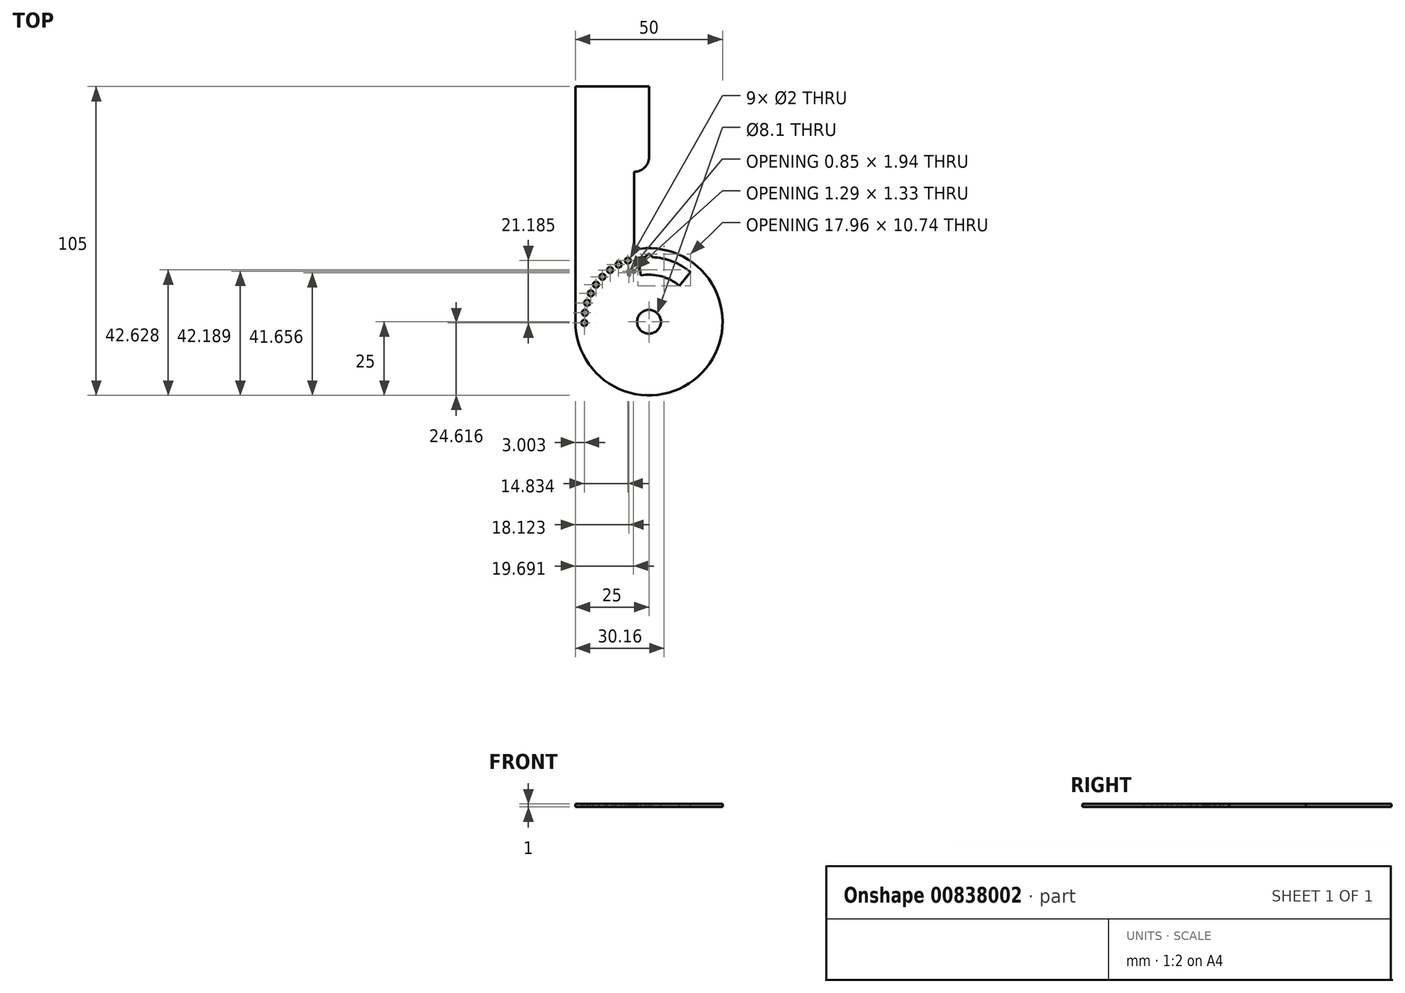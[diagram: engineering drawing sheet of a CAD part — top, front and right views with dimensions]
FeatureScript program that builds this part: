
annotation { "Feature Type Name" : "Feature", "Feature Type Description" : "" }
export const myFeature = defineFeature(function(context is Context, id is Id, definition is map)
    precondition{}
    {
        {
            var Q0;
            Q0=qCreatedBy(makeId("Top.planeOp"),FACE);
            var sketch = newSketch(context, id + "F0", { "sketchPlane" : qUnion([Q0])});
            skCircle(sketch, "E0", {"center": v(0, 0) * mm, "radius": 4.05 * mm});
            skCircle(sketch, "E1", {"center": v(0, 0) * mm, "radius": 25 * mm});
            skLineSegment(sketch, "E2.bottom", {"start": v(-25, 0) * mm, "end": v(25, 0) * mm});
            skLineSegment(sketch, "E2.top", {"start": v(-25, 80) * mm, "end": v(25, 80) * mm});
            skLineSegment(sketch, "E2.left", {"start": v(-25, 0) * mm, "end": v(-25, 80) * mm});
            skLineSegment(sketch, "E2.right", {"start": v(25, 0) * mm, "end": v(25, 80) * mm});
            skLineSegment(sketch, "E3.bottom", {"start": v(25, 65) * mm, "end": v(0, 65) * mm});
            skLineSegment(sketch, "E3.left", {"start": v(25, 65) * mm, "end": v(25, 35) * mm});
            skLineSegment(sketch, "E3.right", {"start": v(0, 65) * mm, "end": v(0, 60) * mm});
            skLineSegment(sketch, "E4", {"start": v(0, 60) * mm, "end": v(25, 35) * mm});
            skSolve(sketch);
        }
        {
            var Q0;
            {var subQ7=sQuery(id+"F0.wireOp",EDGE,"E2.top");Q0=makeQuery(id+"F0.imprint","IMPRINT",FACE,{"disambiguationData":[TD([[makeQuery(id+"F0.imprint","IMPRINT",EDGE,{"derivedFrom":subQ7}),-1.0]])]});}
            var Q1;
            {var subQ0=sQuery(id+"F0.wireOp",EDGE,"E2.bottom");var subQ1=sQuery(id+"F0.wireOp",EDGE,"E0");var subQ2=makeQuery(id+"F0.imprint","INTERSECT",VERTEX,{"disambiguationData":[OD(0.0)],"derivedFrom":[subQ1,subQ0]});Q1=makeQuery(id+"F0.imprint","IMPRINT",FACE,{"disambiguationData":[TD([[makeQuery(id+"F0.imprint","IMPRINT",EDGE,{"disambiguationData":[TD([[subQ2,1.0]])],"derivedFrom":subQ1}),-1.0]])]});}
            var Q2;
            {var subQ0=sQuery(id+"F0.wireOp",EDGE,"E2.bottom");var subQ1=sQuery(id+"F0.wireOp",EDGE,"E0");var subQ2=makeQuery(id+"F0.imprint","INTERSECT",VERTEX,{"disambiguationData":[OD(0.0)],"derivedFrom":[subQ1,subQ0]});Q2=makeQuery(id+"F0.imprint","IMPRINT",FACE,{"disambiguationData":[TD([[makeQuery(id+"F0.imprint","IMPRINT",EDGE,{"disambiguationData":[TD([[subQ2,-1.0]])],"derivedFrom":subQ1}),-1.0]])]});}
            var Q3;
            Q3=makeQuery(id+"F0.imprint","IMPRINT",FACE,{"disambiguationData":[TD([[makeQuery(id+"F0.imprint","IMPRINT",EDGE,{"derivedFrom":sQuery(id+"F0.wireOp",EDGE,"E3.bottom")}),1.0]])]});
            extrude(context, id + "F1", {"entities" : qUnion([Q0, Q1, Q2, Q3]), "oppositeDirection" : true, "depth" : 1 * mm, "offsetDistance" : 25 * mm});
        }
        {
            var Q0;
            Q0=makeQuery(id+"F1.opExtrude","CAP_FACE",FACE,{"disambiguationData":[OSD([sQuery(id+"F0.wireOp",EDGE,"E0"),sQuery(id+"F0.wireOp",EDGE,"E1"),sQuery(id+"F0.wireOp",EDGE,"E2.top"),sQuery(id+"F0.wireOp",EDGE,"E2.left"),sQuery(id+"F0.wireOp",EDGE,"E2.right"),sQuery(id+"F0.wireOp",EDGE,"E3.bottom"),sQuery(id+"F0.wireOp",EDGE,"E3.right"),sQuery(id+"F0.wireOp",EDGE,"E4")])],"isStart":true});
            var sketch = newSketch(context, id + "F2", { "sketchPlane" : qUnion([Q0])});
            skCircle(sketch, "E5", {"center": v(0, -22) * mm, "radius": 1 * mm});
            skPoint(sketch, "E5.centerSnap0", {"position": v(0, -25) * mm});
            skCircle(sketch, "E6.1.0", {"center": v(3.82, -21.67) * mm, "radius": 1 * mm});
            skCircle(sketch, "E6.2.0", {"center": v(7.52, -20.67) * mm, "radius": 1 * mm});
            skCircle(sketch, "E6.3.0", {"center": v(11, -19.05) * mm, "radius": 1 * mm});
            skCircle(sketch, "E6.4.0", {"center": v(14.14, -16.85) * mm, "radius": 1 * mm});
            skCircle(sketch, "E6.5.0", {"center": v(16.85, -14.14) * mm, "radius": 1 * mm});
            skCircle(sketch, "E6.6.0", {"center": v(19.05, -11) * mm, "radius": 1 * mm});
            skCircle(sketch, "E6.7.0", {"center": v(20.67, -7.52) * mm, "radius": 1 * mm});
            skCircle(sketch, "E6.8.0", {"center": v(21.67, -3.82) * mm, "radius": 1 * mm});
            skCircle(sketch, "E6.9.0", {"center": v(22, 0) * mm, "radius": 1 * mm});
            skCircle(sketch, "E6.10.0", {"center": v(21.67, 3.82) * mm, "radius": 1 * mm});
            skCircle(sketch, "E6.11.0", {"center": v(20.67, 7.52) * mm, "radius": 1 * mm});
            skCircle(sketch, "E6.12.0", {"center": v(19.05, 11) * mm, "radius": 1 * mm});
            skCircle(sketch, "E6.13.0", {"center": v(16.85, 14.14) * mm, "radius": 1 * mm});
            skCircle(sketch, "E6.14.0", {"center": v(14.14, 16.85) * mm, "radius": 1 * mm});
            skCircle(sketch, "E6.15.0", {"center": v(11, 19.05) * mm, "radius": 1 * mm});
            skCircle(sketch, "E6.16.0", {"center": v(7.52, 20.67) * mm, "radius": 1 * mm});
            skCircle(sketch, "E6.17.0", {"center": v(3.82, 21.67) * mm, "radius": 1 * mm});
            skCircle(sketch, "E6.18.0", {"center": v(0, 22) * mm, "radius": 1 * mm});
            skCircle(sketch, "E6.19.0", {"center": v(-3.82, 21.67) * mm, "radius": 1 * mm});
            skCircle(sketch, "E6.20.0", {"center": v(-7.52, 20.67) * mm, "radius": 1 * mm});
            skCircle(sketch, "E6.21.0", {"center": v(-11, 19.05) * mm, "radius": 1 * mm});
            skCircle(sketch, "E6.22.0", {"center": v(-14.14, 16.85) * mm, "radius": 1 * mm});
            skCircle(sketch, "E6.23.0", {"center": v(-16.85, 14.14) * mm, "radius": 1 * mm});
            skCircle(sketch, "E6.24.0", {"center": v(-19.05, 11) * mm, "radius": 1 * mm});
            skCircle(sketch, "E6.25.0", {"center": v(-20.67, 7.52) * mm, "radius": 1 * mm});
            skCircle(sketch, "E6.26.0", {"center": v(-21.67, 3.82) * mm, "radius": 1 * mm});
            skCircle(sketch, "E6.27.0", {"center": v(-22, 0) * mm, "radius": 1 * mm});
            skCircle(sketch, "E6.28.0", {"center": v(-21.67, -3.82) * mm, "radius": 1 * mm});
            skCircle(sketch, "E6.29.0", {"center": v(-20.67, -7.52) * mm, "radius": 1 * mm});
            skCircle(sketch, "E6.30.0", {"center": v(-19.05, -11) * mm, "radius": 1 * mm});
            skCircle(sketch, "E6.31.0", {"center": v(-16.85, -14.14) * mm, "radius": 1 * mm});
            skCircle(sketch, "E6.32.0", {"center": v(-14.14, -16.85) * mm, "radius": 1 * mm});
            skCircle(sketch, "E6.33.0", {"center": v(-11, -19.05) * mm, "radius": 1 * mm});
            skCircle(sketch, "E6.34.0", {"center": v(-7.52, -20.67) * mm, "radius": 1 * mm});
            skCircle(sketch, "E6.35.0", {"center": v(-3.82, -21.67) * mm, "radius": 1 * mm});
            skPoint(sketch, "E6.center", {"position": v(0, 0) * mm});
            skSolve(sketch);
        }
        {
            var Q0;
            Q0=makeQuery(id+"F1.opExtrude","CAP_FACE",FACE,{"disambiguationData":[OSD([sQuery(id+"F0.wireOp",EDGE,"E0"),sQuery(id+"F0.wireOp",EDGE,"E1"),sQuery(id+"F0.wireOp",EDGE,"E2.top"),sQuery(id+"F0.wireOp",EDGE,"E2.left"),sQuery(id+"F0.wireOp",EDGE,"E2.right"),sQuery(id+"F0.wireOp",EDGE,"E3.bottom"),sQuery(id+"F0.wireOp",EDGE,"E3.right"),sQuery(id+"F0.wireOp",EDGE,"E4")])],"isStart":true});
            var sketch = newSketch(context, id + "F3", { "sketchPlane" : qUnion([Q0])});
            skText(sketch, "E7", { "text": "0", "fontName": "OpenSans-Regular.ttf"});
            const initialGuessF3  = {"E7": [-0.00082, 0.018, 1, 0, 0.002]};
            skSetInitialGuess(sketch, initialGuessF3);
            skSolve(sketch);
        }
        {
            var Q0;
            {var subQ0=sQuery(id+"F0.wireOp",EDGE,"E2.left");var subQ1=sQuery(id+"F0.wireOp",EDGE,"E4");var subQ2=sQuery(id+"F0.wireOp",EDGE,"E0");var subQ3=sQuery(id+"F0.wireOp",EDGE,"E3.right");var subQ4=sQuery(id+"F0.wireOp",EDGE,"E2.right");var subQ5=sQuery(id+"F0.wireOp",EDGE,"E2.top");var subQ6=sQuery(id+"F0.wireOp",EDGE,"E1");var subQ7=sQuery(id+"F0.wireOp",EDGE,"E3.bottom");Q0=makeQuery(id+"FzcUJQ9qazke6Ee_1.boolean.opBoolean","SPLIT",FACE,{"disambiguationData":[TD([makeQuery(id+"F1.opExtrude","SWEPT_FACE",FACE,{"disambiguationData":[OSD([subQ2])]})])],"derivedFrom":makeQuery(id+"F1.opExtrude","CAP_FACE",FACE,{"disambiguationData":[OSD([subQ2,subQ6,subQ5,subQ0,subQ4,subQ7,subQ3,subQ1])],"isStart":true})});}
            var sketch = newSketch(context, id + "F4", { "sketchPlane" : qUnion([Q0])});
            skText(sketch, "E8", { "text": "45", "fontName": "OpenSans-Regular.ttf"});
            skText(sketch, "E9", { "text": "90", "fontName": "OpenSans-Regular.ttf"});
            skLineSegment(sketch, "E10", {"start": v(0, 0) * mm, "end": v(12.73, 12.73) * mm, "construction": true});
            skLineSegment(sketch, "E11", {"start": v(0, 0) * mm, "end": v(4.05, 0) * mm, "construction": true});
            const initialGuessF4  = {"E8": [0.0116, 0.01386, 0.7071, -0.7071, 0.002], "E9": [0.018, 0.0016, 0, -1, 0.002]};
            skSetInitialGuess(sketch, initialGuessF4);
            skSolve(sketch);
        }
        {
            var Q0;
            Q0=makeQuery(id+"F2.imprint","IMPRINT",FACE,{"disambiguationData":[TD([[makeQuery(id+"F2.imprint","IMPRINT",EDGE,{"derivedFrom":sQuery(id+"F2.wireOp",EDGE,"E5")}),-1.0]])]});
            var sketch = newSketch(context, id + "F5", { "sketchPlane" : qUnion([Q0])});
            skCircle(sketch, "E12", {"center": v(0, 0) * mm, "radius": 22 * mm});
            skLineSegment(sketch, "E13", {"start": v(0, 0) * mm, "end": v(-3.82, 21.67) * mm});
            skCircle(sketch, "E14", {"center": v(0, 0) * mm, "radius": 16 * mm});
            skCircle(sketch, "E15.0", {"center": v(0, 0) * mm, "radius": 4.05 * mm, "construction": true});
            skLineSegment(sketch, "E16", {"start": v(0, 0) * mm, "end": v(0, 4.05) * mm, "construction": true});
            skLineSegment(sketch, "E17", {"start": v(0, 0) * mm, "end": v(14.14, 16.85) * mm});
            skSolve(sketch);
        }
        {
            var Q0;
            Q0=makeQuery(id+"F1.opExtrude","CAP_FACE",FACE,{"disambiguationData":[OSD([sQuery(id+"F0.wireOp",EDGE,"E0"),sQuery(id+"F0.wireOp",EDGE,"E1"),sQuery(id+"F0.wireOp",EDGE,"E2.top"),sQuery(id+"F0.wireOp",EDGE,"E2.left"),sQuery(id+"F0.wireOp",EDGE,"E2.right"),sQuery(id+"F0.wireOp",EDGE,"E3.bottom"),sQuery(id+"F0.wireOp",EDGE,"E3.right"),sQuery(id+"F0.wireOp",EDGE,"E4")])],"isStart":true});
            var sketch = newSketch(context, id + "F6", { "sketchPlane" : qUnion([Q0])});
            skCircle(sketch, "E18", {"center": v(0, 0) * mm, "radius": 22 * mm});
            skCircle(sketch, "E19", {"center": v(-7.16, 20.8) * mm, "radius": 1 * mm});
            skLineSegment(sketch, "E20", {"start": v(0, 22) * mm, "end": v(0, 0) * mm});
            skLineSegment(sketch, "E21", {"start": v(0, 0) * mm, "end": v(-7.16, 20.8) * mm, "construction": true});
            skCircle(sketch, "E22", {"center": v(-10.33, 19.42) * mm, "radius": 1 * mm});
            skCircle(sketch, "E23", {"center": v(-13.24, 17.57) * mm, "radius": 1 * mm});
            skCircle(sketch, "E24", {"center": v(-15.83, 15.28) * mm, "radius": 1 * mm});
            skCircle(sketch, "E25", {"center": v(-18.02, 12.62) * mm, "radius": 1 * mm});
            skLineSegment(sketch, "E26", {"start": v(-18.02, 12.62) * mm, "end": v(0, 0) * mm, "construction": true});
            skLineSegment(sketch, "E27", {"start": v(-15.83, 15.28) * mm, "end": v(0, 0) * mm, "construction": true});
            skLineSegment(sketch, "E28", {"start": v(-13.24, 17.57) * mm, "end": v(0, 0) * mm, "construction": true});
            skLineSegment(sketch, "E29", {"start": v(-10.33, 19.42) * mm, "end": v(0, 0) * mm, "construction": true});
            skCircle(sketch, "E30", {"center": v(-19.77, 9.64) * mm, "radius": 1 * mm});
            skCircle(sketch, "E31", {"center": v(-21.04, 6.43) * mm, "radius": 1 * mm});
            skCircle(sketch, "E32", {"center": v(-21.79, 3.06) * mm, "radius": 1 * mm});
            skCircle(sketch, "E33", {"center": v(-22, -0.38) * mm, "radius": 1 * mm});
            skLineSegment(sketch, "E34", {"start": v(-22, -0.38) * mm, "end": v(0, 0) * mm, "construction": true});
            skLineSegment(sketch, "E35", {"start": v(-21.79, 3.06) * mm, "end": v(0, 0) * mm, "construction": true});
            skLineSegment(sketch, "E36", {"start": v(0, 0) * mm, "end": v(-21.04, 6.43) * mm, "construction": true});
            skLineSegment(sketch, "E37", {"start": v(0, 0) * mm, "end": v(-19.77, 9.64) * mm, "construction": true});
            skCircle(sketch, "E38", {"center": v(0, 22) * mm, "radius": 1 * mm});
            skSolve(sketch);
        }
        {
            var Q0;
            {var subQ0=sQuery(id+"F6.wireOp",EDGE,"E25");var subQ1=sQuery(id+"F6.wireOp",EDGE,"E18");var subQ2=makeQuery(id+"F6.imprint","INTERSECT",VERTEX,{"disambiguationData":[OD(0.0)],"derivedFrom":[subQ1,subQ0]});Q0=makeQuery(id+"F6.imprint","IMPRINT",FACE,{"disambiguationData":[TD([[makeQuery(id+"F6.imprint","IMPRINT",EDGE,{"disambiguationData":[TD([[subQ2,-1.0]])],"derivedFrom":subQ1}),1.0]])]});}
            var Q1;
            {var subQ0=sQuery(id+"F6.wireOp",EDGE,"E25");var subQ1=sQuery(id+"F6.wireOp",EDGE,"E18");var subQ2=makeQuery(id+"F6.imprint","INTERSECT",VERTEX,{"disambiguationData":[OD(0.0)],"derivedFrom":[subQ1,subQ0]});Q1=makeQuery(id+"F6.imprint","IMPRINT",FACE,{"disambiguationData":[TD([[makeQuery(id+"F6.imprint","IMPRINT",EDGE,{"disambiguationData":[TD([[subQ2,-1.0]])],"derivedFrom":subQ1}),-1.0]])]});}
            var Q2;
            {var subQ0=sQuery(id+"F6.wireOp",EDGE,"E24");var subQ1=sQuery(id+"F6.wireOp",EDGE,"E18");var subQ2=makeQuery(id+"F6.imprint","INTERSECT",VERTEX,{"disambiguationData":[OD(0.0)],"derivedFrom":[subQ1,subQ0]});Q2=makeQuery(id+"F6.imprint","IMPRINT",FACE,{"disambiguationData":[TD([[makeQuery(id+"F6.imprint","IMPRINT",EDGE,{"disambiguationData":[TD([[subQ2,-1.0]])],"derivedFrom":subQ1}),-1.0]])]});}
            var Q3;
            {var subQ0=sQuery(id+"F6.wireOp",EDGE,"E24");var subQ1=sQuery(id+"F6.wireOp",EDGE,"E18");var subQ2=makeQuery(id+"F6.imprint","INTERSECT",VERTEX,{"disambiguationData":[OD(0.0)],"derivedFrom":[subQ1,subQ0]});Q3=makeQuery(id+"F6.imprint","IMPRINT",FACE,{"disambiguationData":[TD([[makeQuery(id+"F6.imprint","IMPRINT",EDGE,{"disambiguationData":[TD([[subQ2,-1.0]])],"derivedFrom":subQ1}),1.0]])]});}
            var Q4;
            {var subQ0=sQuery(id+"F6.wireOp",EDGE,"E23");var subQ1=sQuery(id+"F6.wireOp",EDGE,"E18");var subQ2=makeQuery(id+"F6.imprint","INTERSECT",VERTEX,{"disambiguationData":[OD(0.0)],"derivedFrom":[subQ1,subQ0]});Q4=makeQuery(id+"F6.imprint","IMPRINT",FACE,{"disambiguationData":[TD([[makeQuery(id+"F6.imprint","IMPRINT",EDGE,{"disambiguationData":[TD([[subQ2,-1.0]])],"derivedFrom":subQ1}),1.0]])]});}
            var Q5;
            {var subQ0=sQuery(id+"F6.wireOp",EDGE,"E23");var subQ1=sQuery(id+"F6.wireOp",EDGE,"E18");var subQ2=makeQuery(id+"F6.imprint","INTERSECT",VERTEX,{"disambiguationData":[OD(0.0)],"derivedFrom":[subQ1,subQ0]});Q5=makeQuery(id+"F6.imprint","IMPRINT",FACE,{"disambiguationData":[TD([[makeQuery(id+"F6.imprint","IMPRINT",EDGE,{"disambiguationData":[TD([[subQ2,-1.0]])],"derivedFrom":subQ1}),-1.0]])]});}
            var Q6;
            {var subQ0=sQuery(id+"F6.wireOp",EDGE,"E22");var subQ1=sQuery(id+"F6.wireOp",EDGE,"E18");var subQ2=makeQuery(id+"F6.imprint","INTERSECT",VERTEX,{"disambiguationData":[OD(0.0)],"derivedFrom":[subQ1,subQ0]});Q6=makeQuery(id+"F6.imprint","IMPRINT",FACE,{"disambiguationData":[TD([[makeQuery(id+"F6.imprint","IMPRINT",EDGE,{"disambiguationData":[TD([[subQ2,-1.0]])],"derivedFrom":subQ1}),-1.0]])]});}
            var Q7;
            {var subQ0=sQuery(id+"F6.wireOp",EDGE,"E22");var subQ1=sQuery(id+"F6.wireOp",EDGE,"E18");var subQ2=makeQuery(id+"F6.imprint","INTERSECT",VERTEX,{"disambiguationData":[OD(0.0)],"derivedFrom":[subQ1,subQ0]});Q7=makeQuery(id+"F6.imprint","IMPRINT",FACE,{"disambiguationData":[TD([[makeQuery(id+"F6.imprint","IMPRINT",EDGE,{"disambiguationData":[TD([[subQ2,-1.0]])],"derivedFrom":subQ1}),1.0]])]});}
            var Q8;
            {var subQ0=sQuery(id+"F6.wireOp",EDGE,"E19");var subQ1=sQuery(id+"F6.wireOp",EDGE,"E18");var subQ2=makeQuery(id+"F6.imprint","INTERSECT",VERTEX,{"disambiguationData":[OD(0.0)],"derivedFrom":[subQ1,subQ0]});Q8=makeQuery(id+"F6.imprint","IMPRINT",FACE,{"disambiguationData":[TD([[makeQuery(id+"F6.imprint","IMPRINT",EDGE,{"disambiguationData":[TD([[subQ2,-1.0]])],"derivedFrom":subQ1}),-1.0]])]});}
            var Q9;
            {var subQ0=sQuery(id+"F6.wireOp",EDGE,"E19");var subQ1=sQuery(id+"F6.wireOp",EDGE,"E18");var subQ2=makeQuery(id+"F6.imprint","INTERSECT",VERTEX,{"disambiguationData":[OD(0.0)],"derivedFrom":[subQ1,subQ0]});Q9=makeQuery(id+"F6.imprint","IMPRINT",FACE,{"disambiguationData":[TD([[makeQuery(id+"F6.imprint","IMPRINT",EDGE,{"disambiguationData":[TD([[subQ2,-1.0]])],"derivedFrom":subQ1}),1.0]])]});}
            var Q10;
            {var subQ0=sQuery(id+"F6.wireOp",EDGE,"E30");var subQ1=sQuery(id+"F6.wireOp",EDGE,"E18");var subQ2=makeQuery(id+"F6.imprint","INTERSECT",VERTEX,{"disambiguationData":[OD(0.0)],"derivedFrom":[subQ1,subQ0]});Q10=makeQuery(id+"F6.imprint","IMPRINT",FACE,{"disambiguationData":[TD([[makeQuery(id+"F6.imprint","IMPRINT",EDGE,{"disambiguationData":[TD([[subQ2,-1.0]])],"derivedFrom":subQ1}),-1.0]])]});}
            var Q11;
            {var subQ0=sQuery(id+"F6.wireOp",EDGE,"E30");var subQ1=sQuery(id+"F6.wireOp",EDGE,"E18");var subQ2=makeQuery(id+"F6.imprint","INTERSECT",VERTEX,{"disambiguationData":[OD(0.0)],"derivedFrom":[subQ1,subQ0]});Q11=makeQuery(id+"F6.imprint","IMPRINT",FACE,{"disambiguationData":[TD([[makeQuery(id+"F6.imprint","IMPRINT",EDGE,{"disambiguationData":[TD([[subQ2,-1.0]])],"derivedFrom":subQ1}),1.0]])]});}
            var Q12;
            {var subQ0=sQuery(id+"F6.wireOp",EDGE,"E31");var subQ1=sQuery(id+"F6.wireOp",EDGE,"E18");var subQ2=makeQuery(id+"F6.imprint","INTERSECT",VERTEX,{"disambiguationData":[OD(0.0)],"derivedFrom":[subQ1,subQ0]});Q12=makeQuery(id+"F6.imprint","IMPRINT",FACE,{"disambiguationData":[TD([[makeQuery(id+"F6.imprint","IMPRINT",EDGE,{"disambiguationData":[TD([[subQ2,-1.0]])],"derivedFrom":subQ1}),1.0]])]});}
            var Q13;
            {var subQ0=sQuery(id+"F6.wireOp",EDGE,"E31");var subQ1=sQuery(id+"F6.wireOp",EDGE,"E18");var subQ2=makeQuery(id+"F6.imprint","INTERSECT",VERTEX,{"disambiguationData":[OD(0.0)],"derivedFrom":[subQ1,subQ0]});Q13=makeQuery(id+"F6.imprint","IMPRINT",FACE,{"disambiguationData":[TD([[makeQuery(id+"F6.imprint","IMPRINT",EDGE,{"disambiguationData":[TD([[subQ2,-1.0]])],"derivedFrom":subQ1}),-1.0]])]});}
            var Q14;
            {var subQ0=sQuery(id+"F6.wireOp",EDGE,"E32");var subQ1=sQuery(id+"F6.wireOp",EDGE,"E18");var subQ2=makeQuery(id+"F6.imprint","INTERSECT",VERTEX,{"disambiguationData":[OD(0.0)],"derivedFrom":[subQ1,subQ0]});Q14=makeQuery(id+"F6.imprint","IMPRINT",FACE,{"disambiguationData":[TD([[makeQuery(id+"F6.imprint","IMPRINT",EDGE,{"disambiguationData":[TD([[subQ2,-1.0]])],"derivedFrom":subQ1}),1.0]])]});}
            var Q15;
            {var subQ0=sQuery(id+"F6.wireOp",EDGE,"E32");var subQ1=sQuery(id+"F6.wireOp",EDGE,"E18");var subQ2=makeQuery(id+"F6.imprint","INTERSECT",VERTEX,{"disambiguationData":[OD(0.0)],"derivedFrom":[subQ1,subQ0]});Q15=makeQuery(id+"F6.imprint","IMPRINT",FACE,{"disambiguationData":[TD([[makeQuery(id+"F6.imprint","IMPRINT",EDGE,{"disambiguationData":[TD([[subQ2,-1.0]])],"derivedFrom":subQ1}),-1.0]])]});}
            var Q16;
            {var subQ0=sQuery(id+"F6.wireOp",EDGE,"E33");var subQ1=sQuery(id+"F6.wireOp",EDGE,"E18");var subQ2=makeQuery(id+"F6.imprint","INTERSECT",VERTEX,{"disambiguationData":[OD(0.0)],"derivedFrom":[subQ1,subQ0]});Q16=makeQuery(id+"F6.imprint","IMPRINT",FACE,{"disambiguationData":[TD([[makeQuery(id+"F6.imprint","IMPRINT",EDGE,{"disambiguationData":[TD([[subQ2,-1.0]])],"derivedFrom":subQ1}),1.0]])]});}
            var Q17;
            {var subQ0=sQuery(id+"F6.wireOp",EDGE,"E33");var subQ1=sQuery(id+"F6.wireOp",EDGE,"E18");var subQ2=makeQuery(id+"F6.imprint","INTERSECT",VERTEX,{"disambiguationData":[OD(0.0)],"derivedFrom":[subQ1,subQ0]});Q17=makeQuery(id+"F6.imprint","IMPRINT",FACE,{"disambiguationData":[TD([[makeQuery(id+"F6.imprint","IMPRINT",EDGE,{"disambiguationData":[TD([[subQ2,-1.0]])],"derivedFrom":subQ1}),-1.0]])]});}
            extrude(context, id + "F7", {"entities" : qUnion([Q0, Q1, Q2, Q3, Q4, Q5, Q6, Q7, Q8, Q9, Q10, Q11, Q12, Q13, Q14, Q15, Q16, Q17]), "operationType" : NewBodyOperationType.REMOVE, "endBound" : BoundingType.UP_TO_NEXT, "oppositeDirection" : true, "depth" : 25 * mm, "offsetDistance" : 25 * mm});
        }
        {
            var Q0;
            Q0=makeQuery(id+"F1.opExtrude","CAP_FACE",FACE,{"disambiguationData":[OSD([sQuery(id+"F0.wireOp",EDGE,"E0"),sQuery(id+"F0.wireOp",EDGE,"E1"),sQuery(id+"F0.wireOp",EDGE,"E2.top"),sQuery(id+"F0.wireOp",EDGE,"E2.left"),sQuery(id+"F0.wireOp",EDGE,"E2.right"),sQuery(id+"F0.wireOp",EDGE,"E3.bottom"),sQuery(id+"F0.wireOp",EDGE,"E3.right"),sQuery(id+"F0.wireOp",EDGE,"E4")])],"isStart":false});
            var sketch = newSketch(context, id + "F8", { "sketchPlane" : qUnion([Q0])});
            skText(sketch, "E39", { "text": "+1", "fontName": "OpenSans-Regular.ttf"});
            skLineSegment(sketch, "E40", {"start": v(-5.53, -16.07) * mm, "end": v(0, 0) * mm});
            skLineSegment(sketch, "E41", {"start": v(0, 0) * mm, "end": v(0, -4.05) * mm, "construction": true});
            const initialGuessF8  = {"E39": [-0.00424, -0.01652, -0.94552, 0.32557, 0.002]};
            skSetInitialGuess(sketch, initialGuessF8);
            skSolve(sketch);
        }
        {
            var Q0;
            Q0 = qSketchRegion(id + "F8", true);
            extrude(context, id + "F9", {"entities" : qUnion([Q0]), "operationType" : NewBodyOperationType.REMOVE, "endBound" : BoundingType.UP_TO_NEXT, "oppositeDirection" : true, "depth" : 25 * mm, "offsetDistance" : 25 * mm});
        }
        {
            var Q0;
            {var subQ3=makeQuery(id+"F2.imprint","IMPRINT",EDGE,{"derivedFrom":sQuery(id+"F2.wireOp",EDGE,"E6.14.0")});var subQ5=sQuery(id+"F5.wireOp",EDGE,"E12");var subQ10=makeQuery(id+"F5.imprint","INTERSECT",VERTEX,{"disambiguationData":[OD(1.0)],"derivedFrom":[subQ3,subQ5]});Q0=makeQuery(id+"F5.imprint","IMPRINT",FACE,{"disambiguationData":[TD([[makeQuery(id+"F5.imprint","IMPRINT",EDGE,{"disambiguationData":[TD([[subQ10,-1.0]])],"derivedFrom":subQ5}),1.0]])]});}
            var Q1;
            {var subQ0=sQuery(id+"F5.wireOp",EDGE,"E13");var subQ1=sQuery(id+"F5.wireOp",EDGE,"E12");var subQ2=makeQuery(id+"F5.imprint","INTERSECT",VERTEX,{"derivedFrom":[subQ1,subQ0]});Q1=makeQuery(id+"F5.imprint","IMPRINT",FACE,{"disambiguationData":[TD([[makeQuery(id+"F5.imprint","IMPRINT",EDGE,{"disambiguationData":[TD([[subQ2,1.0]])],"derivedFrom":subQ1}),1.0]])]});}
            var Q2;
            {var subQ0=sQuery(id+"F5.wireOp",EDGE,"E12");var subQ1=makeQuery(id+"F2.imprint","IMPRINT",EDGE,{"derivedFrom":sQuery(id+"F2.wireOp",EDGE,"E6.18.0")});var subQ2=makeQuery(id+"F5.imprint","INTERSECT",VERTEX,{"disambiguationData":[OD(0.0)],"derivedFrom":[subQ1,subQ0]});Q2=makeQuery(id+"F5.imprint","IMPRINT",FACE,{"disambiguationData":[TD([[makeQuery(id+"F5.imprint","IMPRINT",EDGE,{"disambiguationData":[TD([[subQ2,-1.0]])],"derivedFrom":subQ0}),1.0]])]});}
            var Q3;
            {var subQ0=sQuery(id+"F5.wireOp",EDGE,"E12");var subQ1=makeQuery(id+"F2.imprint","IMPRINT",EDGE,{"derivedFrom":sQuery(id+"F2.wireOp",EDGE,"E6.17.0")});var subQ2=makeQuery(id+"F5.imprint","INTERSECT",VERTEX,{"disambiguationData":[OD(0.0)],"derivedFrom":[subQ1,subQ0]});Q3=makeQuery(id+"F5.imprint","IMPRINT",FACE,{"disambiguationData":[TD([[makeQuery(id+"F5.imprint","IMPRINT",EDGE,{"disambiguationData":[TD([[subQ2,-1.0]])],"derivedFrom":subQ0}),1.0]])]});}
            var Q4;
            {var subQ0=sQuery(id+"F5.wireOp",EDGE,"E12");var subQ1=makeQuery(id+"F2.imprint","IMPRINT",EDGE,{"derivedFrom":sQuery(id+"F2.wireOp",EDGE,"E6.16.0")});var subQ2=makeQuery(id+"F5.imprint","INTERSECT",VERTEX,{"disambiguationData":[OD(0.0)],"derivedFrom":[subQ1,subQ0]});Q4=makeQuery(id+"F5.imprint","IMPRINT",FACE,{"disambiguationData":[TD([[makeQuery(id+"F5.imprint","IMPRINT",EDGE,{"disambiguationData":[TD([[subQ2,-1.0]])],"derivedFrom":subQ0}),1.0]])]});}
            var Q5;
            {var subQ0=sQuery(id+"F5.wireOp",EDGE,"E12");var subQ1=makeQuery(id+"F2.imprint","IMPRINT",EDGE,{"derivedFrom":sQuery(id+"F2.wireOp",EDGE,"E6.15.0")});var subQ2=makeQuery(id+"F5.imprint","INTERSECT",VERTEX,{"disambiguationData":[OD(0.0)],"derivedFrom":[subQ1,subQ0]});Q5=makeQuery(id+"F5.imprint","IMPRINT",FACE,{"disambiguationData":[TD([[makeQuery(id+"F5.imprint","IMPRINT",EDGE,{"disambiguationData":[TD([[subQ2,-1.0]])],"derivedFrom":subQ0}),1.0]])]});}
            var Q6;
            {var subQ0=sQuery(id+"F5.wireOp",EDGE,"E17");var subQ1=sQuery(id+"F5.wireOp",EDGE,"E12");var subQ2=makeQuery(id+"F5.imprint","INTERSECT",VERTEX,{"derivedFrom":[subQ1,subQ0]});Q6=makeQuery(id+"F5.imprint","IMPRINT",FACE,{"disambiguationData":[TD([[makeQuery(id+"F5.imprint","IMPRINT",EDGE,{"disambiguationData":[TD([[subQ2,-1.0]])],"derivedFrom":subQ1}),1.0]])]});}
            var Q7;
            {var subQ0=sQuery(id+"F5.wireOp",EDGE,"E12");var subQ1=makeQuery(id+"F2.imprint","IMPRINT",EDGE,{"derivedFrom":sQuery(id+"F2.wireOp",EDGE,"E6.18.0")});var subQ2=makeQuery(id+"F5.imprint","INTERSECT",VERTEX,{"disambiguationData":[OD(0.0)],"derivedFrom":[subQ1,subQ0]});Q7=makeQuery(id+"F5.imprint","IMPRINT",FACE,{"disambiguationData":[TD([[makeQuery(id+"F5.imprint","IMPRINT",EDGE,{"disambiguationData":[TD([[subQ2,-1.0]])],"derivedFrom":subQ0}),-1.0]])]});}
            extrude(context, id + "F10", {"entities" : qUnion([Q0, Q1, Q2, Q3, Q4, Q5, Q6, Q7]), "operationType" : NewBodyOperationType.REMOVE, "endBound" : BoundingType.UP_TO_NEXT, "oppositeDirection" : true, "depth" : 25 * mm, "offsetDistance" : 25 * mm});
        }
        {
            var Q0;
            Q0=makeQuery(id+"F1.opExtrude","CAP_FACE",FACE,{"disambiguationData":[OSD([sQuery(id+"F0.wireOp",EDGE,"E0"),sQuery(id+"F0.wireOp",EDGE,"E1"),sQuery(id+"F0.wireOp",EDGE,"E2.top"),sQuery(id+"F0.wireOp",EDGE,"E2.left"),sQuery(id+"F0.wireOp",EDGE,"E2.right"),sQuery(id+"F0.wireOp",EDGE,"E3.bottom"),sQuery(id+"F0.wireOp",EDGE,"E3.right"),sQuery(id+"F0.wireOp",EDGE,"E4")])],"isStart":false});
            var sketch = newSketch(context, id + "F11", { "sketchPlane" : qUnion([Q0])});
            skCircle(sketch, "E42", {"center": v(0, 0) * mm, "radius": 22 * mm, "construction": true});
            skCircle(sketch, "E43", {"center": v(16.95, -14.02) * mm, "radius": 1 * mm});
            skLineSegment(sketch, "E44", {"start": v(0, 0) * mm, "end": v(0, -4.05) * mm, "construction": true});
            skLineSegment(sketch, "E45", {"start": v(16.95, -14.02) * mm, "end": v(0, 0) * mm, "construction": true});
            skCircle(sketch, "E46", {"center": v(19.2, -10.73) * mm, "radius": 1 * mm});
            skLineSegment(sketch, "E47", {"start": v(19.2, -10.73) * mm, "end": v(0, 0) * mm, "construction": true});
            skLineSegment(sketch, "E48", {"start": v(0, 0) * mm, "end": v(20.83, -7.09) * mm, "construction": true});
            skLineSegment(sketch, "E49", {"start": v(0, 0) * mm, "end": v(21.74, -3.34) * mm, "construction": true});
            skCircle(sketch, "E50", {"center": v(20.83, -7.09) * mm, "radius": 1 * mm});
            skCircle(sketch, "E51", {"center": v(21.74, -3.34) * mm, "radius": 1 * mm});
            skSolve(sketch);
        }
        {
            var Q0;
            Q0=makeQuery(id+"F11.imprint","IMPRINT",FACE,{"disambiguationData":[TD([[makeQuery(id+"F11.imprint","IMPRINT",EDGE,{"derivedFrom":sQuery(id+"F11.wireOp",EDGE,"E43")}),-1.0]])]});
            var sketch = newSketch(context, id + "F12", { "sketchPlane" : qUnion([Q0])});
            skCircle(sketch, "E52", {"center": v(0, 0) * mm, "radius": 25 * mm});
            skLineSegment(sketch, "E53", {"start": v(-5, -24.5) * mm, "end": v(-5, -51) * mm});
            skArc(sketch, "E54", {"start": v(0, -56) * mm, "mid": v(-1.46, -52.46) * mm, "end": v(-5, -51) * mm});
            skLineSegment(sketch, "E55", {"start": v(0, -56) * mm, "end": v(0, -80) * mm});
            skSolve(sketch);
        }
        {
            var Q0;
            {var subQ1=sQuery(id+"F12.wireOp",EDGE,"E53");Q0=makeQuery(id+"F12.imprint","IMPRINT",FACE,{"disambiguationData":[TD([[makeQuery(id+"F12.imprint","IMPRINT",EDGE,{"derivedFrom":subQ1}),1.0]])]});}
            extrude(context, id + "F13", {"entities" : qUnion([Q0]), "operationType" : NewBodyOperationType.REMOVE, "endBound" : BoundingType.UP_TO_NEXT, "oppositeDirection" : true, "depth" : 25 * mm, "offsetDistance" : 25 * mm});
        }
    });
